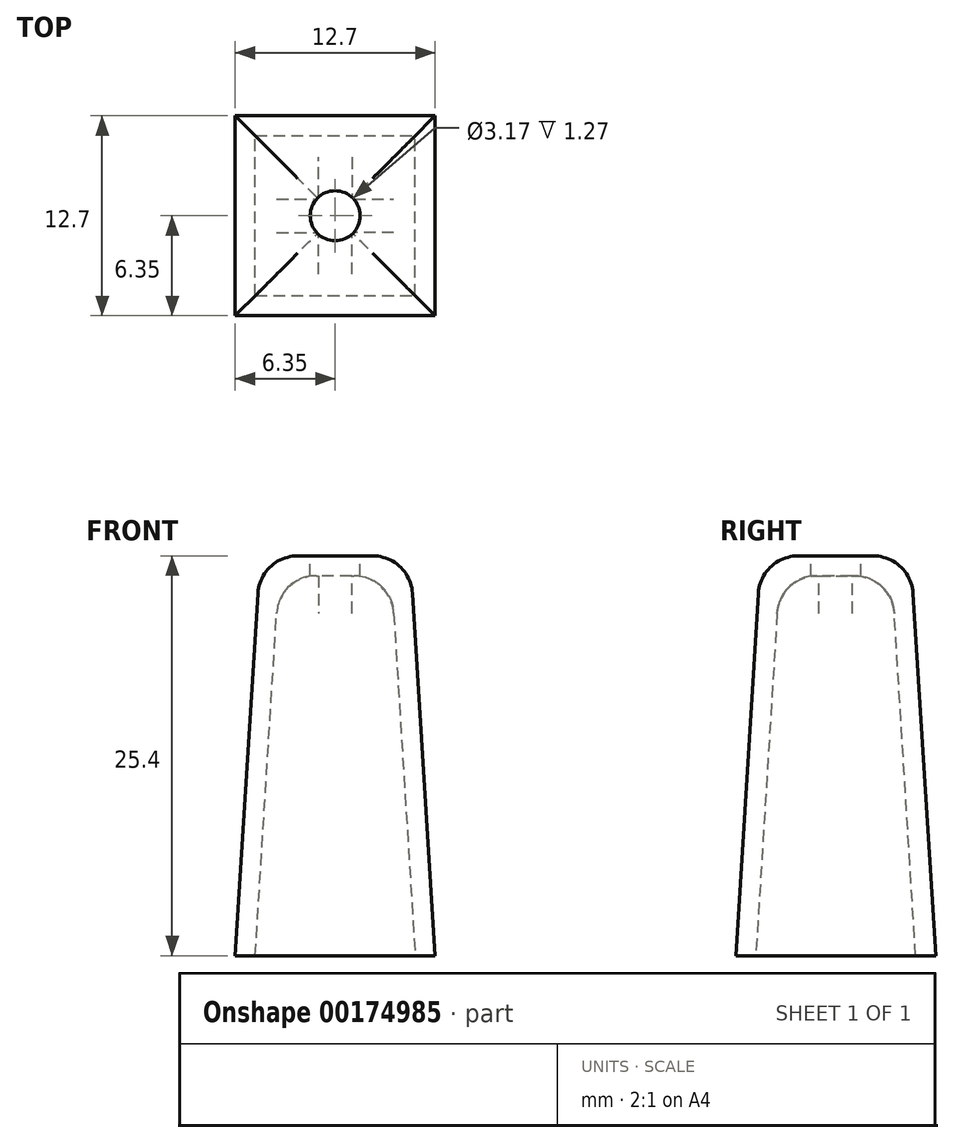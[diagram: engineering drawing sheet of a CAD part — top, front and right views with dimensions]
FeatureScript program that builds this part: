
annotation { "Feature Type Name" : "Feature", "Feature Type Description" : "" }
export const myFeature = defineFeature(function(context is Context, id is Id, definition is map)
    precondition{}
    {
        {
            var Q0;
            Q0=qCreatedBy(makeId("Top.planeOp"),FACE);
            var sketch = newSketch(context, id + "F0", { "sketchPlane" : qUnion([Q0])});
            skLineSegment(sketch, "E0.bottom", {"start": v(0, 0) * mm, "end": v(12.7, 0) * mm});
            skLineSegment(sketch, "E0.top", {"start": v(0, 12.7) * mm, "end": v(12.7, 12.7) * mm});
            skLineSegment(sketch, "E0.left", {"start": v(0, 0) * mm, "end": v(0, 12.7) * mm});
            skLineSegment(sketch, "E0.right", {"start": v(12.7, 0) * mm, "end": v(12.7, 12.7) * mm});
            skSolve(sketch);
        }
        {
            var Q0;
            Q0=qCreatedBy(makeId("Top.planeOp"),FACE);
            cPlane(context, id + "F1", {"entities" : qUnion([Q0]), "cplaneType" : CPlaneType.OFFSET, "offset" : 25.4 * mm, "width" : 152.4 * mm, "height" : 152.4 * mm});
        }
        {
            var Q0;
            Q0=qCreatedBy(id+"F1.planeOp",FACE);
            var sketch = newSketch(context, id + "F2", { "sketchPlane" : qUnion([Q0])});
            skLineSegment(sketch, "E1.bottom", {"start": v(1.59, 1.59) * mm, "end": v(11.11, 1.59) * mm});
            skLineSegment(sketch, "E1.top", {"start": v(1.59, 11.11) * mm, "end": v(11.11, 11.11) * mm});
            skLineSegment(sketch, "E1.left", {"start": v(1.59, 1.59) * mm, "end": v(1.59, 11.11) * mm});
            skLineSegment(sketch, "E1.right", {"start": v(11.11, 1.59) * mm, "end": v(11.11, 11.11) * mm});
            skLineSegment(sketch, "E2", {"start": v(6.35, 11.11) * mm, "end": v(6.35, 12.7) * mm, "construction": true});
            skLineSegment(sketch, "E3", {"start": v(1.59, 6.35) * mm, "end": v(0, 6.35) * mm, "construction": true});
            skLineSegment(sketch, "E4", {"start": v(11.11, 6.35) * mm, "end": v(12.7, 6.35) * mm, "construction": true});
            skLineSegment(sketch, "E5", {"start": v(6.35, 1.59) * mm, "end": v(6.35, 0) * mm, "construction": true});
            skSolve(sketch);
        }
        {
            var Q0;
            Q0=makeQuery(id+"F0.imprint","IMPRINT",FACE,{"disambiguationData":[TD([[makeQuery(id+"F0.imprint","IMPRINT",EDGE,{"derivedFrom":sQuery(id+"F0.wireOp",EDGE,"E0.bottom")}),1.0]])]});
            var Q1;
            Q1=makeQuery(id+"F2.imprint","IMPRINT",FACE,{"disambiguationData":[TD([[makeQuery(id+"F2.imprint","IMPRINT",EDGE,{"derivedFrom":sQuery(id+"F2.wireOp",EDGE,"E1.bottom")}),1.0]])]});
            loft(context, id + "F3", {"sheetProfilesArray" : [{ "sheetProfileEntities" : qUnion([Q0]) }, { "sheetProfileEntities" : qUnion([Q1]) }]});
        }
        {
            var Q0;
            Q0=makeQuery(id+"F3.opLoft","CAP_FACE",FACE,{"disambiguationData":[OSD([makeQuery(id+"F0.imprint","IMPRINT",FACE,{"disambiguationData":[TD([[makeQuery(id+"F0.imprint","IMPRINT",EDGE,{"derivedFrom":sQuery(id+"F0.wireOp",EDGE,"E0.bottom")}),1.0]])]})])],"isStart":true});
            shell(context, id + "F4", {"entities" : qUnion([Q0]), "thickness" : 1.27 * mm});
        }
        {
            var Q0;
            Q0=makeQuery(id+"F3.opLoft","CAP_FACE",FACE,{"disambiguationData":[OSD([makeQuery(id+"F2.imprint","IMPRINT",FACE,{"disambiguationData":[TD([[makeQuery(id+"F2.imprint","IMPRINT",EDGE,{"derivedFrom":sQuery(id+"F2.wireOp",EDGE,"E1.bottom")}),1.0]])]})])],"isStart":true});
            var sketch = newSketch(context, id + "F5", { "sketchPlane" : qUnion([Q0])});
            skLineSegment(sketch, "E6", {"start": v(1.59, 6.35) * mm, "end": v(11.11, 6.35) * mm, "construction": true});
            skLineSegment(sketch, "E7", {"start": v(6.35, 1.59) * mm, "end": v(6.35, 11.11) * mm, "construction": true});
            skCircle(sketch, "E8", {"center": v(6.35, 6.35) * mm, "radius": 1.59 * mm});
            skSolve(sketch);
        }
        {
            var Q0;
            Q0 = qSketchRegion(id + "F5", true);
            extrude(context, id + "F6", {"entities" : qUnion([Q0]), "operationType" : NewBodyOperationType.REMOVE, "oppositeDirection" : true, "depth" : 25.4 * mm});
        }
        {
            var Q0;
            Q0=makeQuery(id+"F3.opLoft","MID_CAP_EDGE",EDGE,{"disambiguationData":[OSD([sQuery(id+"F2.wireOp",EDGE,"E1.top"),sQuery(id+"F2.wireOp",EDGE,"E1.left"),sQuery(id+"F2.wireOp",EDGE,"E1.right")])],"capPos":1.0});
            var Q1;
            Q1=makeQuery(id+"F3.opLoft","MID_CAP_EDGE",EDGE,{"disambiguationData":[OSD([sQuery(id+"F2.wireOp",EDGE,"E1.bottom"),sQuery(id+"F2.wireOp",EDGE,"E1.top"),sQuery(id+"F2.wireOp",EDGE,"E1.right")])],"capPos":1.0});
            var Q2;
            Q2=makeQuery(id+"F3.opLoft","MID_CAP_EDGE",EDGE,{"disambiguationData":[OSD([sQuery(id+"F2.wireOp",EDGE,"E1.bottom"),sQuery(id+"F2.wireOp",EDGE,"E1.left"),sQuery(id+"F2.wireOp",EDGE,"E1.right")])],"capPos":1.0});
            var Q3;
            Q3=makeQuery(id+"F3.opLoft","MID_CAP_EDGE",EDGE,{"disambiguationData":[OSD([sQuery(id+"F2.wireOp",EDGE,"E1.bottom"),sQuery(id+"F2.wireOp",EDGE,"E1.top"),sQuery(id+"F2.wireOp",EDGE,"E1.left")])],"capPos":1.0});
            var Q4;
            Q4=makeQuery(id+"F4.opShell","OFFSET_EDGE",EDGE,{"disambiguationData":[OSD([sQuery(id+"F2.wireOp",EDGE,"E1.top"),sQuery(id+"F2.wireOp",EDGE,"E1.left"),sQuery(id+"F2.wireOp",EDGE,"E1.right")])]});
            var Q5;
            Q5=makeQuery(id+"F4.opShell","OFFSET_EDGE",EDGE,{"disambiguationData":[OSD([sQuery(id+"F2.wireOp",EDGE,"E1.bottom"),sQuery(id+"F2.wireOp",EDGE,"E1.top"),sQuery(id+"F2.wireOp",EDGE,"E1.left")])]});
            var Q6;
            Q6=makeQuery(id+"F4.opShell","OFFSET_EDGE",EDGE,{"disambiguationData":[OSD([sQuery(id+"F2.wireOp",EDGE,"E1.bottom"),sQuery(id+"F2.wireOp",EDGE,"E1.left"),sQuery(id+"F2.wireOp",EDGE,"E1.right")])]});
            var Q7;
            Q7=makeQuery(id+"F4.opShell","OFFSET_EDGE",EDGE,{"disambiguationData":[OSD([sQuery(id+"F2.wireOp",EDGE,"E1.bottom"),sQuery(id+"F2.wireOp",EDGE,"E1.top"),sQuery(id+"F2.wireOp",EDGE,"E1.right")])]});
            fillet(context, id + "F7", {"entities" : qUnion([Q0, Q1, Q2, Q3, Q4, Q5, Q6, Q7]), "radius" : 2.54 * mm, "tangentPropagation" : true, "allowEdgeOverflow" : false});
        }
    });
